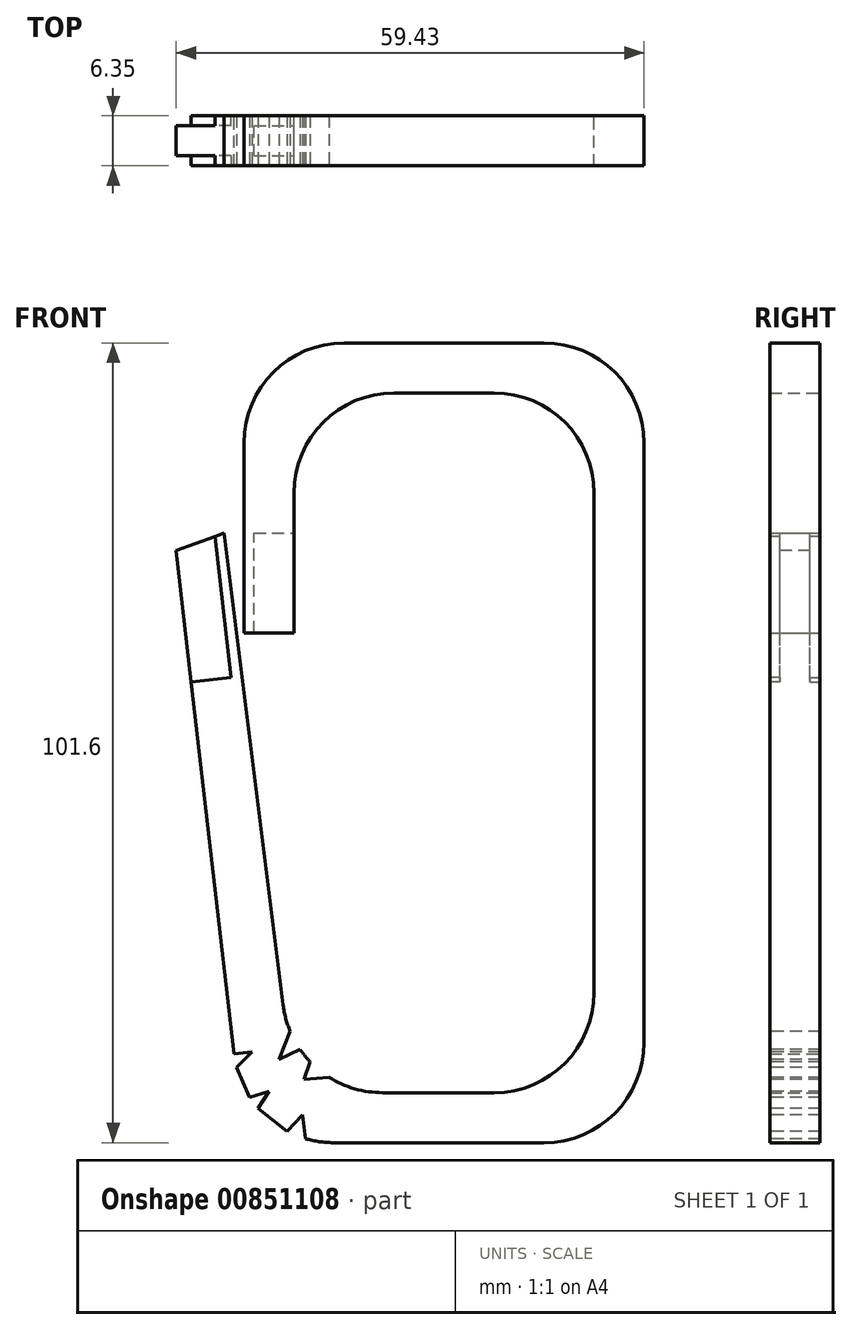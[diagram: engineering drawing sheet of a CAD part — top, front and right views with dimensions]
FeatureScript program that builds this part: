
annotation { "Feature Type Name" : "Feature", "Feature Type Description" : "" }
export const myFeature = defineFeature(function(context is Context, id is Id, definition is map)
    precondition{}
    {
        {
            var Q0;
            Q0=qCreatedBy(makeId("Front.planeOp"),FACE);
            var sketch = newSketch(context, id + "F0", { "sketchPlane" : qUnion([Q0])});
            skLineSegment(sketch, "E0.bottom", {"start": v(25.4, -50.8) * mm, "end": v(-25.4, -50.8) * mm});
            skLineSegment(sketch, "E0.top", {"start": v(25.4, 50.8) * mm, "end": v(-25.4, 50.8) * mm});
            skLineSegment(sketch, "E0.left", {"start": v(25.4, -50.8) * mm, "end": v(25.4, 50.8) * mm});
            skPoint(sketch, "E0.middle", {"position": v(0, 0) * mm});
            skLineSegment(sketch, "E1.bottom", {"start": v(19.05, -44.45) * mm, "end": v(-19.05, -44.45) * mm});
            skLineSegment(sketch, "E1.top", {"start": v(19.05, 44.45) * mm, "end": v(-19.05, 44.45) * mm});
            skLineSegment(sketch, "E1.left", {"start": v(19.05, -44.45) * mm, "end": v(19.05, 44.45) * mm});
            skLineSegment(sketch, "E2", {"start": v(-25.4, -50.8) * mm, "end": v(-34.3, 26.66) * mm});
            skLineSegment(sketch, "E3", {"start": v(-34.3, 26.66) * mm, "end": v(-27.94, 26.66) * mm});
            skLineSegment(sketch, "E4", {"start": v(-27.94, 26.66) * mm, "end": v(-19.05, -44.45) * mm});
            skLineSegment(sketch, "E5", {"start": v(-25.4, 50.8) * mm, "end": v(-25.4, 13.96) * mm});
            skLineSegment(sketch, "E6", {"start": v(-25.4, 13.96) * mm, "end": v(-19.05, 13.96) * mm});
            skLineSegment(sketch, "E7", {"start": v(-19.05, 13.96) * mm, "end": v(-19.05, 44.45) * mm});
            skSolve(sketch);
        }
        {
            var Q0;
            Q0 = qSketchRegion(id + "F0", true);
            extrude(context, id + "F1", {"entities" : qUnion([Q0]), "depth" : 6.35 * mm, "offsetDistance" : 25.4 * mm});
        }
        {
            var Q0;
            Q0=makeQuery(id+"F1.opExtrude","SWEPT_EDGE",EDGE,{"disambiguationData":[OSD([sQuery(id+"F0.wireOp",EDGE,"E1.top"),sQuery(id+"F0.wireOp",EDGE,"E1.right")])]});
            var Q1;
            Q1=makeQuery(id+"F1.opExtrude","SWEPT_EDGE",EDGE,{"disambiguationData":[OSD([sQuery(id+"F0.wireOp",EDGE,"E1.top"),sQuery(id+"F0.wireOp",EDGE,"E1.left")])]});
            var Q2;
            Q2=makeQuery(id+"F1.opExtrude","SWEPT_EDGE",EDGE,{"disambiguationData":[OSD([sQuery(id+"F0.wireOp",EDGE,"E1.bottom"),sQuery(id+"F0.wireOp",EDGE,"E1.left")])]});
            var Q3;
            Q3=makeQuery(id+"F1.opExtrude","SWEPT_EDGE",EDGE,{"disambiguationData":[OSD([sQuery(id+"F0.wireOp",EDGE,"E1.bottom"),sQuery(id+"F0.wireOp",EDGE,"E1.right")])]});
            var Q4;
            Q4=makeQuery(id+"F1.opExtrude","SWEPT_EDGE",EDGE,{"disambiguationData":[OSD([sQuery(id+"F0.wireOp",EDGE,"E0.top"),sQuery(id+"F0.wireOp",EDGE,"E0.right")])]});
            var Q5;
            Q5=makeQuery(id+"F1.opExtrude","SWEPT_EDGE",EDGE,{"disambiguationData":[OSD([sQuery(id+"F0.wireOp",EDGE,"E0.top"),sQuery(id+"F0.wireOp",EDGE,"E0.left")])]});
            var Q6;
            Q6=makeQuery(id+"F1.opExtrude","SWEPT_EDGE",EDGE,{"disambiguationData":[OSD([sQuery(id+"F0.wireOp",EDGE,"E0.bottom"),sQuery(id+"F0.wireOp",EDGE,"E0.left")])]});
            var Q7;
            Q7=makeQuery(id+"F1.opExtrude","SWEPT_EDGE",EDGE,{"disambiguationData":[OSD([sQuery(id+"F0.wireOp",EDGE,"E0.bottom"),sQuery(id+"F0.wireOp",EDGE,"E0.right")])]});
            fillet(context, id + "F2", {"entities" : qUnion([Q0, Q1, Q2, Q3, Q4, Q5, Q6, Q7]), "radius" : 12.7 * mm, "tangentPropagation" : true, "allowEdgeOverflow" : false});
        }
        {
            var Q0;
            Q0=makeQuery(id+"F1.opExtrude","SWEPT_FACE",FACE,{"disambiguationData":[OSD([sQuery(id+"F0.wireOp",EDGE,"E7")])]});
            var sketch = newSketch(context, id + "F3", { "sketchPlane" : qUnion([Q0])});
            skLineSegment(sketch, "E8.0", {"start": v(-6.35, 13.96) * mm, "end": v(-6.35, 31.75) * mm, "construction": true});
            skLineSegment(sketch, "E9.0", {"start": v(0, 31.75) * mm, "end": v(-6.35, 31.75) * mm, "construction": true});
            skLineSegment(sketch, "E10.0", {"start": v(0, 13.96) * mm, "end": v(0, 31.75) * mm, "construction": true});
            skLineSegment(sketch, "E11.0", {"start": v(-6.35, 13.96) * mm, "end": v(0, 13.96) * mm, "construction": true});
            skLineSegment(sketch, "E12.bottom", {"start": v(-5.08, 13.96) * mm, "end": v(-1.27, 13.96) * mm});
            skLineSegment(sketch, "E12.top", {"start": v(-5.08, 26.66) * mm, "end": v(-1.27, 26.66) * mm});
            skLineSegment(sketch, "E12.left", {"start": v(-5.08, 13.96) * mm, "end": v(-5.08, 26.66) * mm});
            skLineSegment(sketch, "E12.right", {"start": v(-1.27, 13.96) * mm, "end": v(-1.27, 26.66) * mm});
            skSolve(sketch);
        }
        {
            var Q0;
            Q0 = qSketchRegion(id + "F3", true);
            extrude(context, id + "F4", {"entities" : qUnion([Q0]), "operationType" : NewBodyOperationType.REMOVE, "oppositeDirection" : true, "depth" : 5.08 * mm, "offsetDistance" : 25.4 * mm});
        }
        {
            var Q0;
            Q0=makeQuery(id+"F1.opExtrude","SWEPT_FACE",FACE,{"disambiguationData":[OSD([sQuery(id+"F0.wireOp",EDGE,"E2")])]});
            var sketch = newSketch(context, id + "F5", { "sketchPlane" : qUnion([Q0])});
            skPoint(sketch, "E13.0", {"position": v(6.35, 30.4) * mm});
            skLineSegment(sketch, "E14.0", {"start": v(6.35, 30.4) * mm, "end": v(0, 30.4) * mm, "construction": true});
            skLineSegment(sketch, "E15.0", {"start": v(6.35, -36.25) * mm, "end": v(6.35, 30.4) * mm, "construction": true});
            skLineSegment(sketch, "E16.0", {"start": v(0, -36.25) * mm, "end": v(0, 30.4) * mm, "construction": true});
            skLineSegment(sketch, "E17.bottom", {"start": v(1.27, 30.4) * mm, "end": v(5.08, 30.4) * mm, "construction": true});
            skLineSegment(sketch, "E17.top", {"start": v(1.27, 11.35) * mm, "end": v(5.08, 11.35) * mm, "construction": true});
            skLineSegment(sketch, "E17.left", {"start": v(1.27, 30.4) * mm, "end": v(1.27, 11.35) * mm, "construction": true});
            skLineSegment(sketch, "E17.right", {"start": v(5.08, 30.4) * mm, "end": v(5.08, 11.35) * mm, "construction": true});
            skLineSegment(sketch, "E18", {"start": v(1.27, 30.4) * mm, "end": v(0, 30.4) * mm});
            skLineSegment(sketch, "E19", {"start": v(1.27, 11.35) * mm, "end": v(1.27, 30.4) * mm});
            skLineSegment(sketch, "E20", {"start": v(1.27, 11.35) * mm, "end": v(0, 11.35) * mm});
            skLineSegment(sketch, "E21", {"start": v(0, 11.35) * mm, "end": v(0, 30.4) * mm});
            skLineSegment(sketch, "E22", {"start": v(5.08, 30.4) * mm, "end": v(6.35, 30.4) * mm});
            skLineSegment(sketch, "E23", {"start": v(5.08, 11.35) * mm, "end": v(6.35, 11.35) * mm});
            skLineSegment(sketch, "E24", {"start": v(6.35, 11.35) * mm, "end": v(6.35, 30.4) * mm});
            skLineSegment(sketch, "E25", {"start": v(5.08, 11.35) * mm, "end": v(5.08, 30.4) * mm});
            skSolve(sketch);
        }
        {
            var Q0;
            Q0 = qSketchRegion(id + "F5", true);
            extrude(context, id + "F6", {"entities" : qUnion([Q0]), "operationType" : NewBodyOperationType.REMOVE, "oppositeDirection" : true, "depth" : 5.08 * mm, "offsetDistance" : 25.4 * mm});
        }
        {
            var Q0;
            Q0=makeQuery(id+"F1.opExtrude","CAP_FACE",FACE,{"disambiguationData":[OSD([sQuery(id+"F0.wireOp",EDGE,"E0.bottom"),sQuery(id+"F0.wireOp",EDGE,"E0.top"),sQuery(id+"F0.wireOp",EDGE,"E0.left"),sQuery(id+"F0.wireOp",EDGE,"E1.bottom"),sQuery(id+"F0.wireOp",EDGE,"E1.top"),sQuery(id+"F0.wireOp",EDGE,"E1.left"),sQuery(id+"F0.wireOp",EDGE,"E2"),sQuery(id+"F0.wireOp",EDGE,"E3"),sQuery(id+"F0.wireOp",EDGE,"E4"),sQuery(id+"F0.wireOp",EDGE,"E5"),sQuery(id+"F0.wireOp",EDGE,"E6"),sQuery(id+"F0.wireOp",EDGE,"E7")])],"isStart":false});
            var sketch = newSketch(context, id + "F7", { "sketchPlane" : qUnion([Q0])});
            skArc(sketch, "E26.0", {"start": v(-26.7, -39.55) * mm, "mid": v(-22.53, -47.58) * mm, "end": v(-14.07, -50.8) * mm, "construction": true});
            skArc(sketch, "E27.0", {"start": v(-7.84, -44.45) * mm, "mid": v(-16.24, -41.27) * mm, "end": v(-20.44, -33.33) * mm, "construction": true});
            skLineSegment(sketch, "E28.0", {"start": v(6.35, -44.45) * mm, "end": v(-7.84, -44.45) * mm, "construction": true});
            skLineSegment(sketch, "E29.0", {"start": v(12.7, -50.8) * mm, "end": v(-14.07, -50.8) * mm, "construction": true});
            skLineSegment(sketch, "E30.0", {"start": v(-26.7, -39.55) * mm, "end": v(-32.12, 7.74) * mm, "construction": true});
            skLineSegment(sketch, "E31.0", {"start": v(-27.94, 26.66) * mm, "end": v(-20.44, -33.33) * mm, "construction": true});
            skLineSegment(sketch, "E32", {"start": v(-26.7, -39.55) * mm, "end": v(-24.4, -39.28) * mm});
            skLineSegment(sketch, "E33", {"start": v(-24.4, -39.28) * mm, "end": v(-26.38, -41.23) * mm});
            skLineSegment(sketch, "E34", {"start": v(-26.38, -41.23) * mm, "end": v(-24.69, -45.08) * mm});
            skLineSegment(sketch, "E35", {"start": v(-24.69, -45.08) * mm, "end": v(-22.23, -44.26) * mm});
            skLineSegment(sketch, "E36", {"start": v(-22.23, -44.26) * mm, "end": v(-23.62, -46.47) * mm});
            skLineSegment(sketch, "E37", {"start": v(-23.62, -46.47) * mm, "end": v(-19.93, -49.37) * mm});
            skLineSegment(sketch, "E38", {"start": v(-19.93, -49.37) * mm, "end": v(-18, -47.26) * mm});
            skLineSegment(sketch, "E39", {"start": v(-18, -47.26) * mm, "end": v(-17.62, -50.3) * mm});
            skLineSegment(sketch, "E40", {"start": v(-17.62, -50.3) * mm, "end": v(-17.62, -52.34) * mm});
            skLineSegment(sketch, "E41", {"start": v(-17.62, -52.34) * mm, "end": v(-33.76, -46.47) * mm});
            skLineSegment(sketch, "E42", {"start": v(-33.76, -46.47) * mm, "end": v(-32.56, -39.55) * mm});
            skLineSegment(sketch, "E43", {"start": v(-32.56, -39.55) * mm, "end": v(-26.7, -39.55) * mm});
            skLineSegment(sketch, "E44", {"start": v(-19.56, -36.65) * mm, "end": v(-20.94, -40.24) * mm});
            skLineSegment(sketch, "E45", {"start": v(-20.94, -40.24) * mm, "end": v(-18.29, -38.97) * mm});
            skLineSegment(sketch, "E46", {"start": v(-18.29, -38.97) * mm, "end": v(-17, -40.54) * mm});
            skLineSegment(sketch, "E47", {"start": v(-17, -40.54) * mm, "end": v(-17.8, -42.75) * mm});
            skLineSegment(sketch, "E48", {"start": v(-17.8, -42.75) * mm, "end": v(-14.62, -42.5) * mm});
            skLineSegment(sketch, "E49", {"start": v(-14.62, -42.5) * mm, "end": v(-13.13, -40.96) * mm});
            skLineSegment(sketch, "E50", {"start": v(-13.13, -40.96) * mm, "end": v(-18.08, -35.23) * mm});
            skLineSegment(sketch, "E51", {"start": v(-18.08, -35.23) * mm, "end": v(-19.56, -36.65) * mm});
            skSolve(sketch);
        }
        {
            var Q0;
            Q0 = qSketchRegion(id + "F7", true);
            extrude(context, id + "F8", {"entities" : qUnion([Q0]), "operationType" : NewBodyOperationType.REMOVE, "oppositeDirection" : true, "depth" : 25.4 * mm, "offsetDistance" : 25.4 * mm});
        }
        {
            var Q0;
            Q0=makeQuery(id+"F1.opExtrude","CAP_FACE",FACE,{"disambiguationData":[OSD([sQuery(id+"F0.wireOp",EDGE,"E0.bottom"),sQuery(id+"F0.wireOp",EDGE,"E0.top"),sQuery(id+"F0.wireOp",EDGE,"E0.left"),sQuery(id+"F0.wireOp",EDGE,"E1.bottom"),sQuery(id+"F0.wireOp",EDGE,"E1.top"),sQuery(id+"F0.wireOp",EDGE,"E1.left"),sQuery(id+"F0.wireOp",EDGE,"E2"),sQuery(id+"F0.wireOp",EDGE,"E3"),sQuery(id+"F0.wireOp",EDGE,"E4"),sQuery(id+"F0.wireOp",EDGE,"E5"),sQuery(id+"F0.wireOp",EDGE,"E6"),sQuery(id+"F0.wireOp",EDGE,"E7")])],"isStart":false});
            var sketch = newSketch(context, id + "F9", { "sketchPlane" : qUnion([Q0])});
            skLineSegment(sketch, "E52.0", {"start": v(-34.3, 26.66) * mm, "end": v(-29.18, 26.66) * mm, "construction": true});
            skLineSegment(sketch, "E53.0", {"start": v(-32.12, 7.74) * mm, "end": v(-34.3, 26.66) * mm, "construction": true});
            skLineSegment(sketch, "E54.0", {"start": v(-29.18, 26.66) * mm, "end": v(-27.94, 26.66) * mm, "construction": true});
            skLineSegment(sketch, "E55", {"start": v(-34.03, 24.44) * mm, "end": v(-27.94, 26.66) * mm});
            skLineSegment(sketch, "E56", {"start": v(-34.3, 26.66) * mm, "end": v(-34.03, 24.44) * mm});
            skLineSegment(sketch, "E57", {"start": v(-34.3, 26.66) * mm, "end": v(-27.94, 26.66) * mm});
            skSolve(sketch);
        }
        {
            var Q0;
            Q0 = qSketchRegion(id + "F9", true);
            extrude(context, id + "F10", {"entities" : qUnion([Q0]), "operationType" : NewBodyOperationType.REMOVE, "endBound" : BoundingType.THROUGH_ALL, "oppositeDirection" : true, "depth" : 25.4 * mm, "offsetDistance" : 25.4 * mm});
        }
    });
